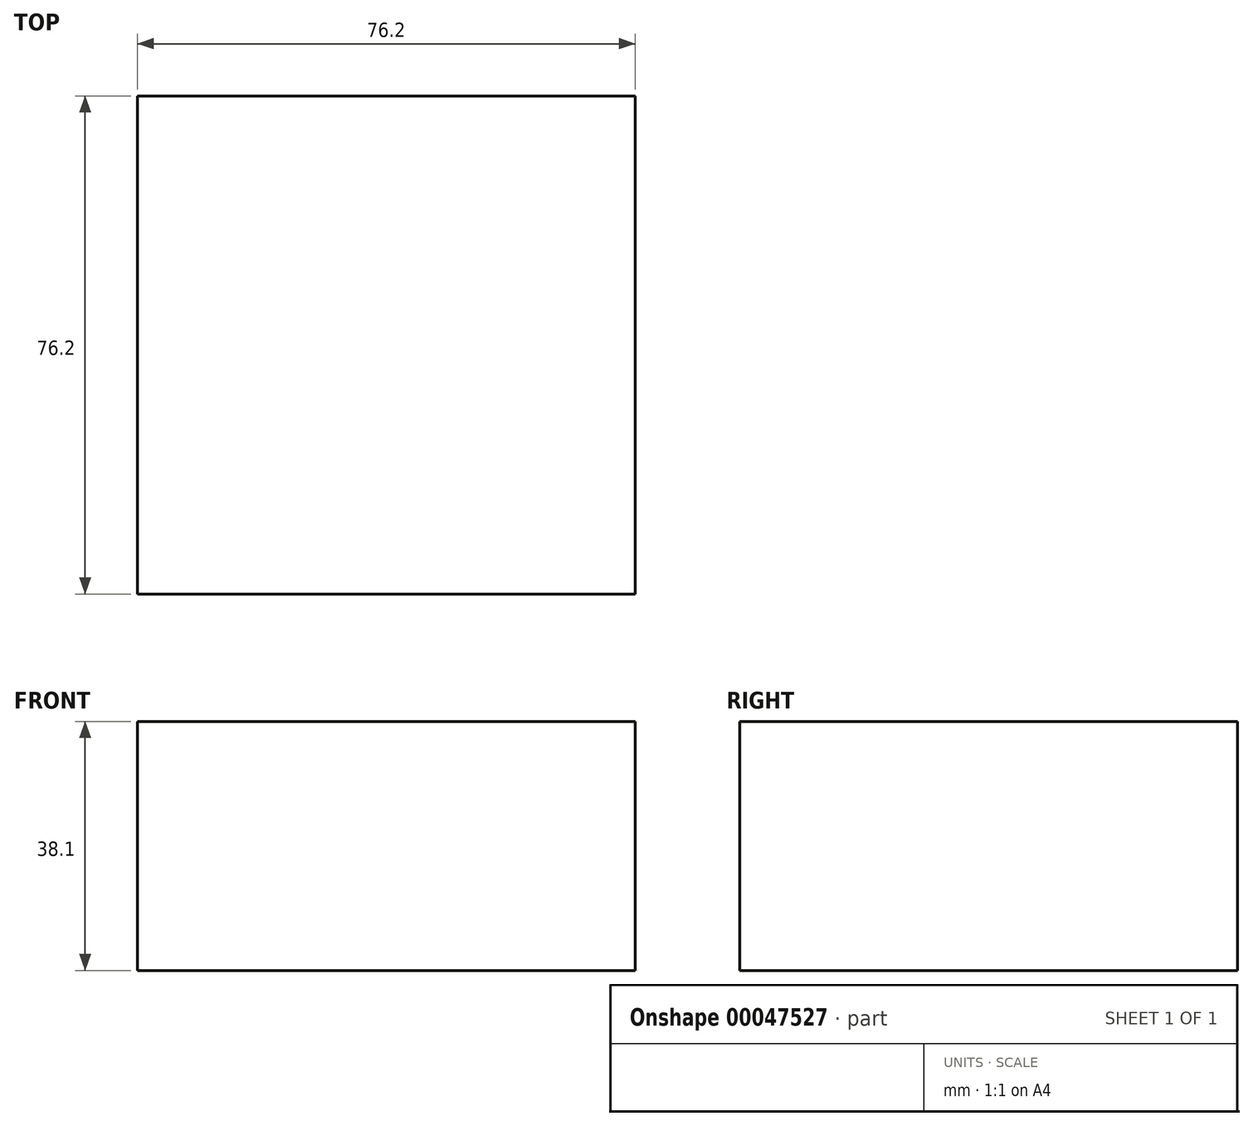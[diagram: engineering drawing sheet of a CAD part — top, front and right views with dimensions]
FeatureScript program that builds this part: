
annotation { "Feature Type Name" : "Feature", "Feature Type Description" : "" }
export const myFeature = defineFeature(function(context is Context, id is Id, definition is map)
    precondition{}
    {
        {
            var Q0;
            Q0=qCreatedBy(makeId("Top.planeOp"),FACE);
            var sketch = newSketch(context, id + "F0", { "sketchPlane" : qUnion([Q0])});
            skLineSegment(sketch, "E0.rect.bottom", {"start": v(38.1, -38.1) * mm, "end": v(-38.1, -38.1) * mm});
            skLineSegment(sketch, "E0.rect.top", {"start": v(38.1, 38.1) * mm, "end": v(-38.1, 38.1) * mm});
            skLineSegment(sketch, "E0.rect.left", {"start": v(38.1, -38.1) * mm, "end": v(38.1, 38.1) * mm});
            skLineSegment(sketch, "E0.rect.right", {"start": v(-38.1, -38.1) * mm, "end": v(-38.1, 38.1) * mm});
            skPoint(sketch, "E0.rect.middle", {"position": v(0, 0) * mm});
            skSolve(sketch);
        }
        {
            var Q0;
            Q0=makeQuery(id+"F0.imprint","IMPRINT",FACE,{"disambiguationData":[TD([[makeQuery(id+"F0.imprint","IMPRINT",EDGE,{"derivedFrom":sQuery(id+"F0.wireOp",EDGE,"E0.rect.bottom")}),-1.0]])]});
            extrude(context, id + "F1", {"entities" : qUnion([Q0]), "depth" : 38.1 * mm});
        }
    });
